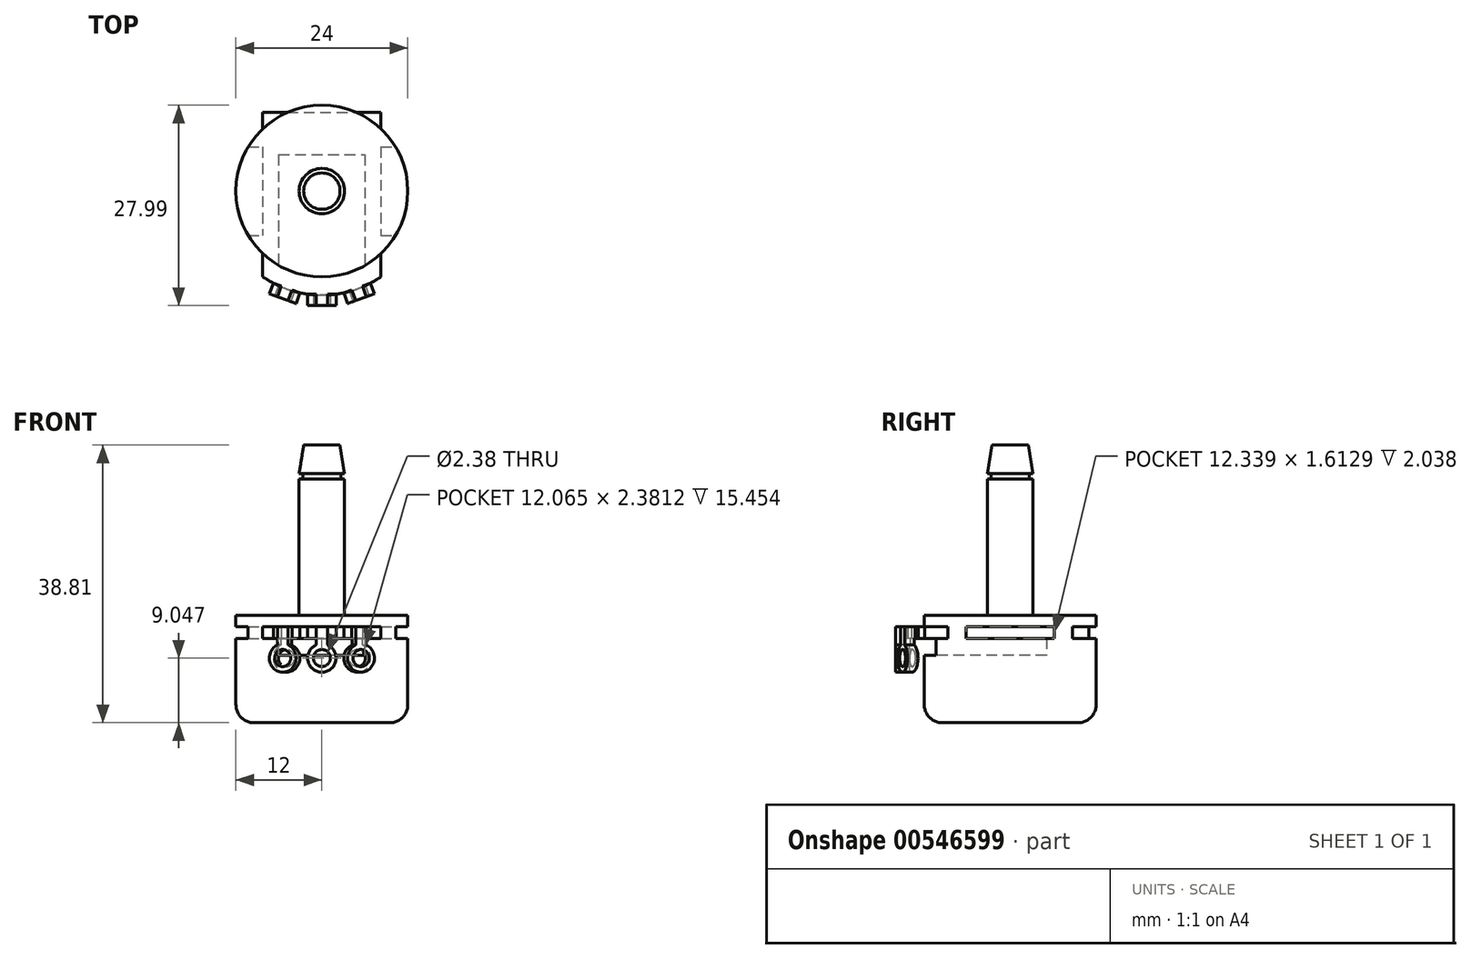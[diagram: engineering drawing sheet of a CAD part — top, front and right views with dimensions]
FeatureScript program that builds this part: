
annotation { "Feature Type Name" : "Feature", "Feature Type Description" : "" }
export const myFeature = defineFeature(function(context is Context, id is Id, definition is map)
    precondition{}
    {
        {
            var Q0;
            Q0=qCreatedBy(makeId("Front.planeOp"),FACE);
            var sketch = newSketch(context, id + "F0", { "sketchPlane" : qUnion([Q0])});
            skLineSegment(sketch, "E0", {"start": v(0, 15) * mm, "end": v(0, 0) * mm});
            skLineSegment(sketch, "E1", {"start": v(0, 0) * mm, "end": v(-12, 0) * mm});
            skLineSegment(sketch, "E2", {"start": v(-12, 0) * mm, "end": v(-12, 15) * mm});
            skLineSegment(sketch, "E3", {"start": v(-12, 15) * mm, "end": v(0, 15) * mm});
            skSolve(sketch);
        }
        {
            var Q0;
            Q0=makeQuery(id+"F0.imprint","IMPRINT",FACE,{"disambiguationData":[TD([[makeQuery(id+"F0.imprint","IMPRINT",EDGE,{"derivedFrom":sQuery(id+"F0.wireOp",EDGE,"E0")}),-1.0]])]});
            var Q1;
            Q1=sQuery(id+"F0.wireOp",EDGE,"E0");
            revolve(context, id + "F1", {"entities" : qUnion([Q0]), "axis" : qUnion([Q1]), "revolveType" : RevolveType.FULL});
        }
        {
            var Q0;
            Q0=makeQuery(id+"F1.opRevolve","SWEPT_EDGE",EDGE,{"disambiguationData":[OSD([sQuery(id+"F0.wireOp",EDGE,"E1"),sQuery(id+"F0.wireOp",EDGE,"E2")])]});
            fillet(context, id + "F2", {"entities" : qUnion([Q0]), "radius" : 2.54 * mm, "tangentPropagation" : true, "allowEdgeOverflow" : false});
        }
        {
            var Q0;
            Q0=qCreatedBy(makeId("Front.planeOp"),FACE);
            var sketch = newSketch(context, id + "F3", { "sketchPlane" : qUnion([Q0])});
            skLineSegment(sketch, "E4.bottom", {"start": v(0, 13.41) * mm, "end": v(-8.26, 13.41) * mm});
            skLineSegment(sketch, "E4.top", {"start": v(0, 11.8) * mm, "end": v(-8.26, 11.8) * mm});
            skLineSegment(sketch, "E4.left", {"start": v(0, 13.41) * mm, "end": v(0, 11.8) * mm});
            skLineSegment(sketch, "E4.right", {"start": v(-8.26, 13.41) * mm, "end": v(-8.26, 11.8) * mm});
            skLineSegment(sketch, "E5.MirrorCS", {"start": v(0, 13.41) * mm, "end": v(8.26, 13.41) * mm});
            skLineSegment(sketch, "E6.MirrorCS", {"start": v(8.26, 13.41) * mm, "end": v(8.26, 11.8) * mm});
            skLineSegment(sketch, "E7.MirrorCS", {"start": v(0, 11.8) * mm, "end": v(8.26, 11.8) * mm});
            skSolve(sketch);
        }
        {
            var Q0;
            Q0=qSketchRegion(id+"F3",true);
            extrude(context, id + "F4", {"entities" : qUnion([Q0]), "operationType" : NewBodyOperationType.REMOVE, "oppositeDirection" : true, "depth" : 25.4 * mm, "symmetric" : true});
        }
        {
            var Q0;
            Q0=qCreatedBy(makeId("Right.planeOp"),FACE);
            var sketch = newSketch(context, id + "F5", { "sketchPlane" : qUnion([Q0])});
            skLineSegment(sketch, "E8.bottom", {"start": v(-6.17, 13.41) * mm, "end": v(6.17, 13.41) * mm});
            skLineSegment(sketch, "E8.top", {"start": v(-6.17, 11.8) * mm, "end": v(6.17, 11.8) * mm});
            skLineSegment(sketch, "E8.left", {"start": v(-6.17, 13.41) * mm, "end": v(-6.17, 11.8) * mm});
            skLineSegment(sketch, "E8.right", {"start": v(6.17, 13.41) * mm, "end": v(6.17, 11.8) * mm});
            skLineSegment(sketch, "E9", {"start": v(0, 0) * mm, "end": v(0, 11.8) * mm});
            skSolve(sketch);
        }
        {
            var Q0;
            Q0=qSketchRegion(id+"F5",true);
            extrude(context, id + "F6", {"entities" : qUnion([Q0]), "operationType" : NewBodyOperationType.REMOVE, "oppositeDirection" : true, "depth" : 25.4 * mm, "symmetric" : true});
        }
        {
            var Q0;
            Q0=qCreatedBy(makeId("Front.planeOp"),FACE);
            var sketch = newSketch(context, id + "F7", { "sketchPlane" : qUnion([Q0])});
            skLineSegment(sketch, "E10.bottom", {"start": v(-6.03, 11.8) * mm, "end": v(6.03, 11.8) * mm});
            skLineSegment(sketch, "E10.top", {"start": v(-6.03, 9.42) * mm, "end": v(6.03, 9.42) * mm});
            skLineSegment(sketch, "E10.left", {"start": v(-6.03, 11.8) * mm, "end": v(-6.03, 9.42) * mm});
            skLineSegment(sketch, "E10.right", {"start": v(6.03, 11.8) * mm, "end": v(6.03, 9.42) * mm});
            skLineSegment(sketch, "E11", {"start": v(0, 11.8) * mm, "end": v(0, 13.41) * mm});
            skSolve(sketch);
        }
        {
            var Q0;
            Q0=qSketchRegion(id+"F7",true);
            extrude(context, id + "F8", {"entities" : qUnion([Q0]), "operationType" : NewBodyOperationType.REMOVE, "oppositeDirection" : true, "depth" : 5.08 * mm, "hasSecondDirection" : true, "secondDirectionOppositeDirection" : false, "secondDirectionDepth" : 25.4 * mm});
        }
        {
            var Q0;
            Q0=makeQuery(id+"F6.boolean.opBoolean","MERGE",FACE,{"derivedFrom":[makeQuery(id+"F4.boolean.opBoolean","COPY",FACE,{"derivedFrom":makeQuery(id+"F4.opExtrude","SWEPT_FACE",FACE,{"disambiguationData":[OSD([sQuery(id+"F3.wireOp",EDGE,"E4.top"),sQuery(id+"F3.wireOp",EDGE,"E7.MirrorCS")])]})}),makeQuery(id+"F6.opExtrude","SWEPT_FACE",FACE,{"disambiguationData":[OSD([sQuery(id+"F5.wireOp",EDGE,"E8.top")])]})]});
            var sketch = newSketch(context, id + "F9", { "sketchPlane" : qUnion([Q0])});
            skLineSegment(sketch, "E12.bottom", {"start": v(-8.26, 10.98) * mm, "end": v(8.26, 10.98) * mm});
            skLineSegment(sketch, "E12.left", {"start": v(-8.26, 10.98) * mm, "end": v(-8.26, -11.97) * mm});
            skLineSegment(sketch, "E12.right", {"start": v(8.26, 10.98) * mm, "end": v(8.26, -11.97) * mm});
            skLineSegment(sketch, "E13", {"start": v(0, 12) * mm, "end": v(0, 10.98) * mm});
            skArc(sketch, "E14", {"start": v(-8.26, -11.97) * mm, "mid": v(0, -14.54) * mm, "end": v(8.26, -11.97) * mm});
            skSolve(sketch);
        }
        {
            var Q0;
            Q0=qSketchRegion(id+"F9",true);
            extrude(context, id + "F10", {"entities" : qUnion([Q0]), "operationType" : NewBodyOperationType.ADD, "depth" : 1.61 * mm});
        }
        {
            var Q0;
            {var subQ0=sQuery(id+"F9.wireOp",EDGE,"E14");var subQ1=sQuery(id+"F9.wireOp",EDGE,"E12.left");var subQ2=sQuery(id+"F9.wireOp",EDGE,"E12.right");Q0=makeQuery(id+"F10.boolean.opBoolean","SPLIT",FACE,{"disambiguationData":[TD([makeQuery(id+"F1.opRevolve","SWEPT_FACE",FACE,{"disambiguationData":[OSD([sQuery(id+"F0.wireOp",EDGE,"E2")])]}),makeQuery(id+"F10.opExtrude","SWEPT_FACE",FACE,{"disambiguationData":[OSD([subQ1])]}),makeQuery(id+"F10.opExtrude","SWEPT_FACE",FACE,{"disambiguationData":[OSD([subQ2])]}),makeQuery(id+"F10.opExtrude","SWEPT_FACE",FACE,{"disambiguationData":[OSD([subQ0])]})])],"derivedFrom":makeQuery(id+"F10.opExtrude","CAP_FACE",FACE,{"disambiguationData":[OSD([sQuery(id+"F9.wireOp",EDGE,"E12.bottom"),subQ1,subQ2,subQ0])],"isStart":false})});}
            var sketch = newSketch(context, id + "F11", { "sketchPlane" : qUnion([Q0])});
            skLineSegment(sketch, "E15", {"start": v(0, -14.54) * mm, "end": v(0, 0) * mm});
            skLineSegment(sketch, "E16", {"start": v(0, 0) * mm, "end": v(4.97, -13.66) * mm});
            skArc(sketch, "E17", {"start": v(3.06, -14.21) * mm, "mid": v(4.97, -13.66) * mm, "end": v(6.8, -12.86) * mm});
            skLineSegment(sketch, "E18", {"start": v(3.06, -14.21) * mm, "end": v(3.6, -15.7) * mm});
            skLineSegment(sketch, "E19", {"start": v(3.6, -15.7) * mm, "end": v(7.33, -14.35) * mm});
            skLineSegment(sketch, "E20", {"start": v(7.33, -14.35) * mm, "end": v(6.8, -12.86) * mm});
            skLineSegment(sketch, "E21.1.0", {"start": v(-1.98, -14.4) * mm, "end": v(-1.98, -16) * mm});
            skArc(sketch, "E21.1.1", {"start": v(-1.98, -14.4) * mm, "mid": v(0, -14.54) * mm, "end": v(1.98, -14.4) * mm});
            skLineSegment(sketch, "E21.1.2", {"start": v(1.98, -16) * mm, "end": v(1.98, -14.4) * mm});
            skLineSegment(sketch, "E21.1.3", {"start": v(-1.98, -16) * mm, "end": v(1.98, -16) * mm});
            skLineSegment(sketch, "E21.2.0", {"start": v(-6.8, -12.86) * mm, "end": v(-7.33, -14.35) * mm});
            skArc(sketch, "E21.2.1", {"start": v(-6.8, -12.86) * mm, "mid": v(-4.97, -13.66) * mm, "end": v(-3.06, -14.21) * mm});
            skLineSegment(sketch, "E21.2.2", {"start": v(-3.6, -15.7) * mm, "end": v(-3.06, -14.21) * mm});
            skLineSegment(sketch, "E21.2.3", {"start": v(-7.33, -14.35) * mm, "end": v(-3.6, -15.7) * mm});
            skLineSegment(sketch, "E21.anchor1", {"start": v(0, 0) * mm, "end": v(3.6, -15.7) * mm, "construction": true});
            skLineSegment(sketch, "E21.anchor2", {"start": v(0, 0) * mm, "end": v(-7.33, -14.35) * mm, "construction": true});
            skSolve(sketch);
        }
        {
            var Q0;
            Q0=qSketchRegion(id+"F11",true);
            extrude(context, id + "F12", {"entities" : qUnion([Q0]), "operationType" : NewBodyOperationType.ADD, "oppositeDirection" : true, "depth" : 6.35 * mm});
        }
        {
            var Q0;
            Q0=makeQuery(id+"F12.opExtrude","SWEPT_FACE",FACE,{"disambiguationData":[OSD([sQuery(id+"F11.wireOp",EDGE,"E19")])]});
            var sketch = newSketch(context, id + "F13", { "sketchPlane" : qUnion([Q0])});
            skCircle(sketch, "E22", {"center": v(0, 9.05) * mm, "radius": 1.2 * mm});
            skCircle(sketch, "E23", {"center": v(0, 9.05) * mm, "radius": 1.98 * mm});
            skLineSegment(sketch, "E24", {"start": v(-0.8, 13.41) * mm, "end": v(-0.8, 10.87) * mm});
            skLineSegment(sketch, "E25", {"start": v(-0.8, 13.41) * mm, "end": v(-1.98, 13.41) * mm});
            skLineSegment(sketch, "E26", {"start": v(-1.98, 13.41) * mm, "end": v(-1.98, 7.06) * mm});
            skLineSegment(sketch, "E27", {"start": v(-1.98, 7.06) * mm, "end": v(1.98, 7.06) * mm});
            skLineSegment(sketch, "E28", {"start": v(1.98, 7.06) * mm, "end": v(1.98, 13.41) * mm});
            skLineSegment(sketch, "E29", {"start": v(1.98, 13.41) * mm, "end": v(0.8, 13.41) * mm});
            skLineSegment(sketch, "E30", {"start": v(0.8, 13.41) * mm, "end": v(0.8, 10.87) * mm});
            skLineSegment(sketch, "E31", {"start": v(0, 13.41) * mm, "end": v(0, 12.39) * mm});
            skSolve(sketch);
        }
        {
            var Q0;
            {var subQ0=sQuery(id+"F13.wireOp",EDGE,"E24");Q0=makeQuery(id+"F13.imprint","IMPRINT",FACE,{"disambiguationData":[TD([[makeQuery(id+"F13.imprint","IMPRINT",EDGE,{"derivedFrom":subQ0}),-1.0]])]});}
            var Q1;
            {var subQ4=sQuery(id+"F13.wireOp",EDGE,"E29");Q1=makeQuery(id+"F13.imprint","IMPRINT",FACE,{"disambiguationData":[TD([[makeQuery(id+"F13.imprint","IMPRINT",EDGE,{"derivedFrom":subQ4}),-1.0]])]});}
            var Q2;
            {var subQ0=sQuery(id+"F13.wireOp",EDGE,"E28");var subQ1=sQuery(id+"F13.wireOp",EDGE,"E23");var subQ2=makeQuery(id+"F13.imprint","INTERSECT",VERTEX,{"derivedFrom":[subQ1,subQ0]});Q2=makeQuery(id+"F13.imprint","IMPRINT",FACE,{"disambiguationData":[TD([[makeQuery(id+"F13.imprint","IMPRINT",EDGE,{"disambiguationData":[TD([[subQ2,1.0]])],"derivedFrom":subQ1}),-1.0]])]});}
            var Q3;
            {var subQ0=sQuery(id+"F13.wireOp",EDGE,"E26");var subQ1=sQuery(id+"F13.wireOp",EDGE,"E23");var subQ2=makeQuery(id+"F13.imprint","INTERSECT",VERTEX,{"derivedFrom":[subQ1,subQ0]});Q3=makeQuery(id+"F13.imprint","IMPRINT",FACE,{"disambiguationData":[TD([[makeQuery(id+"F13.imprint","IMPRINT",EDGE,{"disambiguationData":[TD([[subQ2,-1.0]])],"derivedFrom":subQ1}),-1.0]])]});}
            var Q4;
            Q4=makeQuery(id+"F13.imprint","IMPRINT",FACE,{"disambiguationData":[TD([[makeQuery(id+"F13.imprint","IMPRINT",EDGE,{"derivedFrom":sQuery(id+"F13.wireOp",EDGE,"E22")}),1.0]])]});
            var Q5;
            Q5=makeQuery(id+"F12.opExtrude","CAP_VERTEX",VERTEX,{"disambiguationData":[OSD([sQuery(id+"F9.wireOp",EDGE,"E14"),sQuery(id+"F11.wireOp",EDGE,"E17"),sQuery(id+"F11.wireOp",EDGE,"E18")])],"isStart":true});
            extrude(context, id + "F14", {"entities" : qUnion([Q0, Q1, Q2, Q3, Q4]), "operationType" : NewBodyOperationType.REMOVE, "endBound" : BoundingType.UP_TO_VERTEX, "oppositeDirection" : true, "endBoundEntityVertex" : qUnion([Q5]), "depth" : 25.4 * mm});
        }
        {
            var Q0;
            Q0=makeQuery(id+"F12.opExtrude","SWEPT_FACE",FACE,{"disambiguationData":[OSD([sQuery(id+"F11.wireOp",EDGE,"E21.1.3")])]});
            var sketch = newSketch(context, id + "F15", { "sketchPlane" : qUnion([Q0])});
            skCircle(sketch, "E32", {"center": v(0, 9.05) * mm, "radius": 1.2 * mm});
            skCircle(sketch, "E33", {"center": v(0, 9.05) * mm, "radius": 1.98 * mm});
            skLineSegment(sketch, "E34.bottom", {"start": v(-1.98, 13.41) * mm, "end": v(1.98, 13.41) * mm});
            skLineSegment(sketch, "E34.top", {"start": v(-1.98, 7.06) * mm, "end": v(1.98, 7.06) * mm});
            skLineSegment(sketch, "E34.left", {"start": v(-1.98, 13.41) * mm, "end": v(-1.98, 7.06) * mm});
            skLineSegment(sketch, "E34.right", {"start": v(1.98, 13.41) * mm, "end": v(1.98, 7.06) * mm});
            skLineSegment(sketch, "E35.bottom", {"start": v(-0.8, 13.41) * mm, "end": v(0.8, 13.41) * mm});
            skLineSegment(sketch, "E35.top", {"start": v(-0.8, 10.87) * mm, "end": v(0.8, 10.87) * mm});
            skLineSegment(sketch, "E35.left", {"start": v(-0.8, 13.41) * mm, "end": v(-0.8, 10.87) * mm});
            skLineSegment(sketch, "E35.right", {"start": v(0.8, 13.41) * mm, "end": v(0.8, 10.87) * mm});
            skSolve(sketch);
        }
        {
            var Q0;
            {var subQ0=sQuery(id+"F15.wireOp",EDGE,"E35.left");Q0=makeQuery(id+"F15.imprint","IMPRINT",FACE,{"disambiguationData":[TD([[makeQuery(id+"F15.imprint","IMPRINT",EDGE,{"derivedFrom":subQ0}),-1.0]])]});}
            var Q1;
            {var subQ0=sQuery(id+"F15.wireOp",EDGE,"E35.right");Q1=makeQuery(id+"F15.imprint","IMPRINT",FACE,{"disambiguationData":[TD([[makeQuery(id+"F15.imprint","IMPRINT",EDGE,{"derivedFrom":subQ0}),1.0]])]});}
            var Q2;
            Q2=makeQuery(id+"F15.imprint","IMPRINT",FACE,{"disambiguationData":[TD([[makeQuery(id+"F15.imprint","IMPRINT",EDGE,{"derivedFrom":sQuery(id+"F15.wireOp",EDGE,"E32")}),1.0]])]});
            var Q3;
            {var subQ0=sQuery(id+"F15.wireOp",EDGE,"E34.right");var subQ1=sQuery(id+"F15.wireOp",EDGE,"E33");var subQ2=makeQuery(id+"F15.imprint","INTERSECT",VERTEX,{"derivedFrom":[subQ1,subQ0]});Q3=makeQuery(id+"F15.imprint","IMPRINT",FACE,{"disambiguationData":[TD([[makeQuery(id+"F15.imprint","IMPRINT",EDGE,{"disambiguationData":[TD([[subQ2,1.0]])],"derivedFrom":subQ1}),-1.0]])]});}
            var Q4;
            {var subQ0=sQuery(id+"F15.wireOp",EDGE,"E34.left");var subQ1=sQuery(id+"F15.wireOp",EDGE,"E33");var subQ2=makeQuery(id+"F15.imprint","INTERSECT",VERTEX,{"derivedFrom":[subQ1,subQ0]});Q4=makeQuery(id+"F15.imprint","IMPRINT",FACE,{"disambiguationData":[TD([[makeQuery(id+"F15.imprint","IMPRINT",EDGE,{"disambiguationData":[TD([[subQ2,-1.0]])],"derivedFrom":subQ1}),-1.0]])]});}
            var Q5;
            Q5=makeQuery(id+"F12.opExtrude","CAP_VERTEX",VERTEX,{"disambiguationData":[OSD([sQuery(id+"F9.wireOp",EDGE,"E14"),sQuery(id+"F11.wireOp",EDGE,"E21.1.0"),sQuery(id+"F11.wireOp",EDGE,"E21.1.1")])],"isStart":true});
            extrude(context, id + "F16", {"entities" : qUnion([Q0, Q1, Q2, Q3, Q4]), "operationType" : NewBodyOperationType.REMOVE, "endBound" : BoundingType.UP_TO_VERTEX, "oppositeDirection" : true, "endBoundEntityVertex" : qUnion([Q5]), "depth" : 25.4 * mm});
        }
        {
            var Q0;
            Q0=makeQuery(id+"F12.opExtrude","SWEPT_FACE",FACE,{"disambiguationData":[OSD([sQuery(id+"F11.wireOp",EDGE,"E21.2.3")])]});
            var sketch = newSketch(context, id + "F17", { "sketchPlane" : qUnion([Q0])});
            skCircle(sketch, "E36", {"center": v(0, 9.05) * mm, "radius": 1.98 * mm});
            skCircle(sketch, "E37", {"center": v(0, 9.05) * mm, "radius": 1.2 * mm});
            skLineSegment(sketch, "E38.bottom", {"start": v(-1.98, 13.41) * mm, "end": v(1.98, 13.41) * mm});
            skLineSegment(sketch, "E38.top", {"start": v(-1.98, 7.06) * mm, "end": v(1.98, 7.06) * mm});
            skLineSegment(sketch, "E38.left", {"start": v(-1.98, 13.41) * mm, "end": v(-1.98, 7.06) * mm});
            skLineSegment(sketch, "E38.right", {"start": v(1.98, 13.41) * mm, "end": v(1.98, 7.06) * mm});
            skLineSegment(sketch, "E39.bottom", {"start": v(-0.8, 13.41) * mm, "end": v(0.8, 13.41) * mm});
            skLineSegment(sketch, "E39.top", {"start": v(-0.8, 10.87) * mm, "end": v(0.8, 10.87) * mm});
            skLineSegment(sketch, "E39.left", {"start": v(-0.8, 13.41) * mm, "end": v(-0.8, 10.87) * mm});
            skLineSegment(sketch, "E39.right", {"start": v(0.8, 13.41) * mm, "end": v(0.8, 10.87) * mm});
            skSolve(sketch);
        }
        {
            var Q0;
            {var subQ0=sQuery(id+"F17.wireOp",EDGE,"E39.left");Q0=makeQuery(id+"F17.imprint","IMPRINT",FACE,{"disambiguationData":[TD([[makeQuery(id+"F17.imprint","IMPRINT",EDGE,{"derivedFrom":subQ0}),-1.0]])]});}
            var Q1;
            {var subQ0=sQuery(id+"F17.wireOp",EDGE,"E39.right");Q1=makeQuery(id+"F17.imprint","IMPRINT",FACE,{"disambiguationData":[TD([[makeQuery(id+"F17.imprint","IMPRINT",EDGE,{"derivedFrom":subQ0}),1.0]])]});}
            var Q2;
            Q2=makeQuery(id+"F17.imprint","IMPRINT",FACE,{"disambiguationData":[TD([[makeQuery(id+"F17.imprint","IMPRINT",EDGE,{"derivedFrom":sQuery(id+"F17.wireOp",EDGE,"E37")}),1.0]])]});
            var Q3;
            {var subQ0=sQuery(id+"F17.wireOp",EDGE,"E38.right");var subQ1=sQuery(id+"F17.wireOp",EDGE,"E36");var subQ2=makeQuery(id+"F17.imprint","INTERSECT",VERTEX,{"derivedFrom":[subQ1,subQ0]});Q3=makeQuery(id+"F17.imprint","IMPRINT",FACE,{"disambiguationData":[TD([[makeQuery(id+"F17.imprint","IMPRINT",EDGE,{"disambiguationData":[TD([[subQ2,1.0]])],"derivedFrom":subQ1}),-1.0]])]});}
            var Q4;
            {var subQ0=sQuery(id+"F17.wireOp",EDGE,"E38.left");var subQ1=sQuery(id+"F17.wireOp",EDGE,"E36");var subQ2=makeQuery(id+"F17.imprint","INTERSECT",VERTEX,{"derivedFrom":[subQ1,subQ0]});Q4=makeQuery(id+"F17.imprint","IMPRINT",FACE,{"disambiguationData":[TD([[makeQuery(id+"F17.imprint","IMPRINT",EDGE,{"disambiguationData":[TD([[subQ2,-1.0]])],"derivedFrom":subQ1}),-1.0]])]});}
            var Q5;
            Q5=makeQuery(id+"F12.opExtrude","CAP_VERTEX",VERTEX,{"disambiguationData":[OSD([sQuery(id+"F9.wireOp",EDGE,"E14"),sQuery(id+"F11.wireOp",EDGE,"E21.2.0"),sQuery(id+"F11.wireOp",EDGE,"E21.2.1")])],"isStart":true});
            extrude(context, id + "F18", {"entities" : qUnion([Q0, Q1, Q2, Q3, Q4]), "operationType" : NewBodyOperationType.REMOVE, "endBound" : BoundingType.UP_TO_VERTEX, "oppositeDirection" : true, "endBoundEntityVertex" : qUnion([Q5]), "depth" : 25.4 * mm});
        }
        {
            var Q0;
            Q0=makeQuery(id+"F1.opRevolve","SWEPT_FACE",FACE,{"disambiguationData":[OSD([sQuery(id+"F0.wireOp",EDGE,"E3")])]});
            var sketch = newSketch(context, id + "F19", { "sketchPlane" : qUnion([Q0])});
            skCircle(sketch, "E40", {"center": v(0, 0) * mm, "radius": 3.18 * mm});
            skSolve(sketch);
        }
        {
            var Q0;
            Q0=qSketchRegion(id+"F19",true);
            extrude(context, id + "F20", {"entities" : qUnion([Q0]), "operationType" : NewBodyOperationType.ADD, "depth" : 19.05 * mm});
        }
        {
            var Q0;
            Q0=qCreatedBy(makeId("Front.planeOp"),FACE);
            var sketch = newSketch(context, id + "F21", { "sketchPlane" : qUnion([Q0])});
            skLineSegment(sketch, "E41", {"start": v(0, 34.05) * mm, "end": v(0, 38.81) * mm});
            skLineSegment(sketch, "E42", {"start": v(0, 38.81) * mm, "end": v(2.54, 38.81) * mm});
            skLineSegment(sketch, "E43", {"start": v(2.54, 38.81) * mm, "end": v(3.17, 34.84) * mm});
            skLineSegment(sketch, "E44", {"start": v(3.17, 34.84) * mm, "end": v(3.05, 34.84) * mm});
            skArc(sketch, "E45", {"start": v(3.05, 34.84) * mm, "mid": v(2.65, 34.45) * mm, "end": v(3.05, 34.05) * mm});
            skLineSegment(sketch, "E46", {"start": v(0, 34.05) * mm, "end": v(3.05, 34.05) * mm});
            skSolve(sketch);
        }
        {
            var Q0;
            Q0=qSketchRegion(id+"F21",true);
            var Q1;
            Q1=sQuery(id+"F21.wireOp",EDGE,"E41");
            revolve(context, id + "F22", {"operationType" : NewBodyOperationType.ADD, "entities" : qUnion([Q0]), "axis" : qUnion([Q1]), "revolveType" : RevolveType.FULL});
        }
    });
